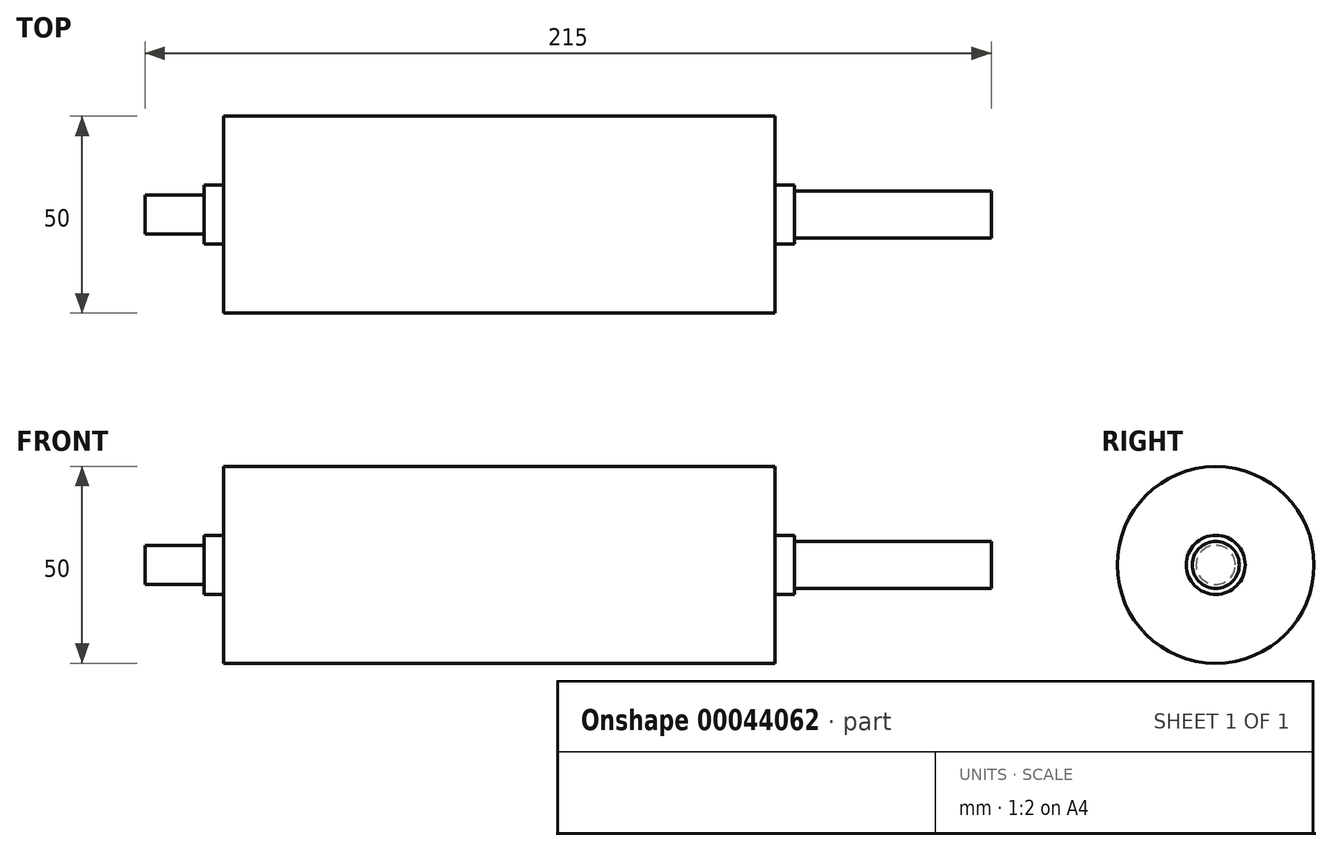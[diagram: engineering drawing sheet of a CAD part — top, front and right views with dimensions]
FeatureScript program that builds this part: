
annotation { "Feature Type Name" : "Feature", "Feature Type Description" : "" }
export const myFeature = defineFeature(function(context is Context, id is Id, definition is map)
    precondition{}
    {
        {
            var Q0;
            Q0=qCreatedBy(makeId("Right.planeOp"),FACE);
            var sketch = newSketch(context, id + "F0", { "sketchPlane" : qUnion([Q0])});
            skCircle(sketch, "E0", {"center": v(0, 0) * mm, "radius": 25 * mm});
            skSolve(sketch);
        }
        {
            var Q0;
            Q0=makeQuery(id+"F0.imprint","IMPRINT",FACE,{"disambiguationData":[TD([[makeQuery(id+"F0.imprint","IMPRINT",EDGE,{"derivedFrom":sQuery(id+"F0.wireOp",EDGE,"E0")}),1.0]])]});
            extrude(context, id + "F1", {"entities" : qUnion([Q0]), "depth" : 70 * mm});
        }
        {
            var Q0;
            Q0=makeQuery(id+"F1.opExtrude","CAP_FACE",FACE,{"disambiguationData":[OSD([sQuery(id+"F0.wireOp",EDGE,"E0")])],"isStart":false});
            var sketch = newSketch(context, id + "F2", { "sketchPlane" : qUnion([Q0])});
            skCircle(sketch, "E1", {"center": v(0, 0) * mm, "radius": 7.5 * mm});
            skSolve(sketch);
        }
        {
            var Q0;
            Q0=makeQuery(id+"F2.imprint","IMPRINT",FACE,{"disambiguationData":[TD([[makeQuery(id+"F2.imprint","IMPRINT",EDGE,{"derivedFrom":sQuery(id+"F2.wireOp",EDGE,"E1")}),1.0]])]});
            extrude(context, id + "F3", {"entities" : qUnion([Q0]), "operationType" : NewBodyOperationType.ADD, "depth" : 5 * mm});
        }
        {
            var Q0;
            Q0=makeQuery(id+"F3.opExtrude","CAP_FACE",FACE,{"disambiguationData":[OSD([sQuery(id+"F2.wireOp",EDGE,"E1")])],"isStart":false});
            var sketch = newSketch(context, id + "F4", { "sketchPlane" : qUnion([Q0])});
            skCircle(sketch, "E2", {"center": v(0, 0) * mm, "radius": 5.97 * mm});
            skSolve(sketch);
        }
        {
            var Q0;
            Q0=makeQuery(id+"F4.imprint","IMPRINT",FACE,{"disambiguationData":[TD([[makeQuery(id+"F4.imprint","IMPRINT",EDGE,{"derivedFrom":sQuery(id+"F4.wireOp",EDGE,"E2")}),1.0]])]});
            extrude(context, id + "F5", {"entities" : qUnion([Q0]), "operationType" : NewBodyOperationType.ADD, "depth" : 50 * mm});
        }
        {
            var Q0;
            Q0=makeQuery(id+"F1.opExtrude","CAP_FACE",FACE,{"disambiguationData":[OSD([sQuery(id+"F0.wireOp",EDGE,"E0")])],"isStart":true});
            extrude(context, id + "F6", {"entities" : qUnion([Q0]), "operationType" : NewBodyOperationType.ADD, "depth" : 70 * mm});
        }
        {
            var Q0;
            Q0=makeQuery(id+"F6.opExtrude","CAP_FACE",FACE,{"disambiguationData":[OSD([sQuery(id+"F0.wireOp",EDGE,"E0")])],"isStart":false});
            var sketch = newSketch(context, id + "F7", { "sketchPlane" : qUnion([Q0])});
            skCircle(sketch, "E3", {"center": v(0, 0) * mm, "radius": 7.5 * mm});
            skSolve(sketch);
        }
        {
            var Q0;
            Q0=makeQuery(id+"F7.imprint","IMPRINT",FACE,{"disambiguationData":[TD([[makeQuery(id+"F7.imprint","IMPRINT",EDGE,{"derivedFrom":sQuery(id+"F7.wireOp",EDGE,"E3")}),1.0]])]});
            extrude(context, id + "F8", {"entities" : qUnion([Q0]), "operationType" : NewBodyOperationType.ADD, "depth" : 5 * mm});
        }
        {
            var Q0;
            Q0=makeQuery(id+"F8.opExtrude","CAP_FACE",FACE,{"disambiguationData":[OSD([sQuery(id+"F7.wireOp",EDGE,"E3")])],"isStart":false});
            var sketch = newSketch(context, id + "F9", { "sketchPlane" : qUnion([Q0])});
            skCircle(sketch, "E4", {"center": v(0, 0) * mm, "radius": 4.97 * mm});
            skSolve(sketch);
        }
        {
            var Q0;
            Q0=makeQuery(id+"F9.imprint","IMPRINT",FACE,{"disambiguationData":[TD([[makeQuery(id+"F9.imprint","IMPRINT",EDGE,{"derivedFrom":sQuery(id+"F9.wireOp",EDGE,"E4")}),1.0]])]});
            extrude(context, id + "F10", {"entities" : qUnion([Q0]), "operationType" : NewBodyOperationType.ADD, "depth" : 15 * mm});
        }
    });
